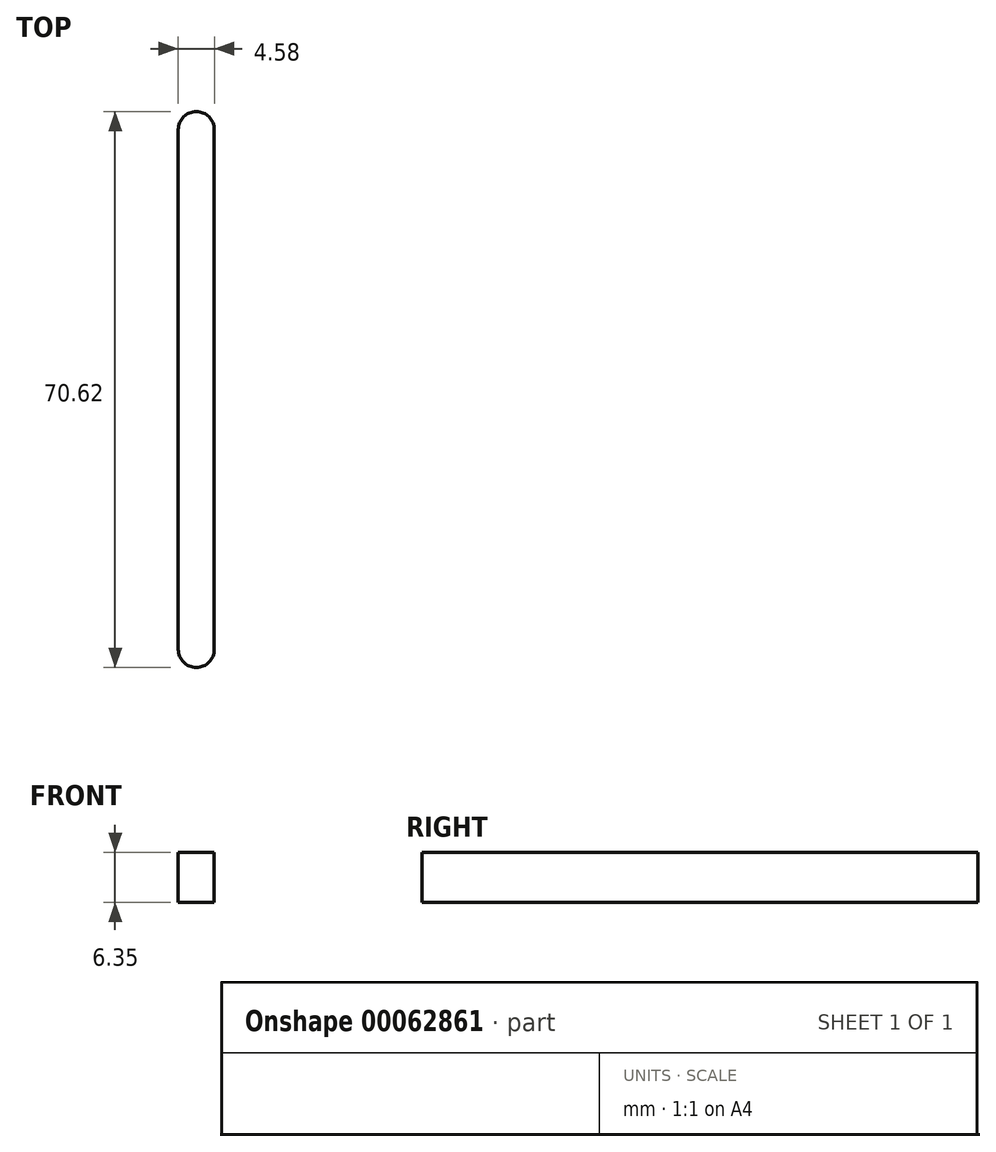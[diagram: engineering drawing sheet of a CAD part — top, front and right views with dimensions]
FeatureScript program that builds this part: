
annotation { "Feature Type Name" : "Feature", "Feature Type Description" : "" }
export const myFeature = defineFeature(function(context is Context, id is Id, definition is map)
    precondition{}
    {
        {
            var Q0;
            Q0=qCreatedBy(makeId("Top.planeOp"),FACE);
            var sketch = newSketch(context, id + "F0", { "sketchPlane" : qUnion([Q0])});
            skLineSegment(sketch, "E0.rect.bottom", {"start": v(3.17, -38.1) * mm, "end": v(-3.18, -38.1) * mm});
            skLineSegment(sketch, "E0.rect.top", {"start": v(3.18, 38.1) * mm, "end": v(-3.17, 38.1) * mm});
            skLineSegment(sketch, "E0.rect.left", {"start": v(3.17, -38.1) * mm, "end": v(3.18, 38.1) * mm});
            skLineSegment(sketch, "E0.rect.right", {"start": v(-3.18, -38.1) * mm, "end": v(-3.17, 38.1) * mm});
            skPoint(sketch, "E0.rect.middle", {"position": v(0, 0) * mm});
            skSolve(sketch);
        }
        {
            var Q0;
            Q0=makeQuery(id+"F0.imprint","IMPRINT",FACE,{"disambiguationData":[TD([[makeQuery(id+"F0.imprint","IMPRINT",EDGE,{"derivedFrom":sQuery(id+"F0.wireOp",EDGE,"E0.rect.bottom")}),-1.0]])]});
            extrude(context, id + "F1", {"entities" : qUnion([Q0]), "depth" : 6.35 * mm});
        }
        {
            var Q0;
            Q0=makeQuery(id+"F1.opExtrude","CAP_FACE",FACE,{"disambiguationData":[OSD([sQuery(id+"F0.wireOp",EDGE,"E0.rect.bottom"),sQuery(id+"F0.wireOp",EDGE,"E0.rect.top"),sQuery(id+"F0.wireOp",EDGE,"E0.rect.left"),sQuery(id+"F0.wireOp",EDGE,"E0.rect.right")])],"isStart":false});
            var sketch = newSketch(context, id + "F2", { "sketchPlane" : qUnion([Q0])});
            skLineSegment(sketch, "E1", {"start": v(0, 33.02) * mm, "end": v(0, -33.02) * mm});
            skArc(sketch, "E2.0.startCap", {"start": v(-2.29, 33.02) * mm, "mid": v(0, 35.3) * mm, "end": v(2.29, 33.02) * mm});
            skArc(sketch, "E2.0.endCap", {"start": v(2.29, -33.02) * mm, "mid": v(0, -35.3) * mm, "end": v(-2.29, -33.02) * mm});
            skLineSegment(sketch, "E2.0.left", {"start": v(2.29, 33.02) * mm, "end": v(2.29, -33.02) * mm});
            skLineSegment(sketch, "E2.0.right", {"start": v(-2.29, 33.02) * mm, "end": v(-2.29, -33.02) * mm});
            skSolve(sketch);
        }
        {
            var Q0;
            Q0=makeQuery(id+"F2.imprint","IMPRINT",FACE,{"disambiguationData":[TD([[makeQuery(id+"F2.imprint","IMPRINT",EDGE,{"derivedFrom":sQuery(id+"F2.wireOp",EDGE,"E2.0.startCap")}),-1.0]])]});
            extrude(context, id + "F3", {"entities" : qUnion([Q0]), "operationType" : NewBodyOperationType.REMOVE, "endBound" : BoundingType.UP_TO_NEXT, "oppositeDirection" : true, "depth" : 25.4 * mm});
        }
    });
